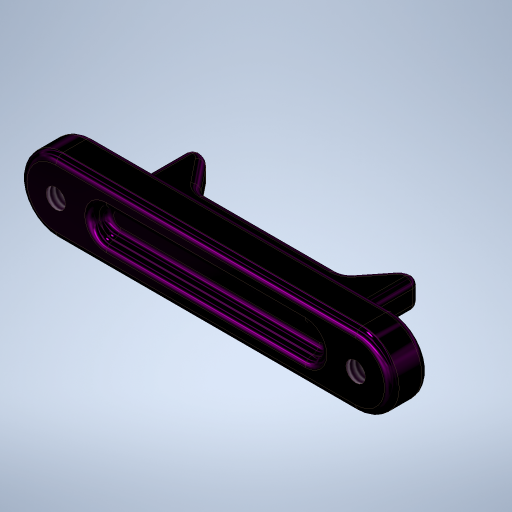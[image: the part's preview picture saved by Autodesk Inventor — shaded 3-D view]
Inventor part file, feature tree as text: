
AUTODESK INVENTOR PART (.ipt)
format: ipt  version: 2023.1 (Build 271208000, 208)  size: 450,560 bytes
history: native  units: in
note: dims shown in document units (in); Inventor stores cm internally (conversion verified against a paired STEP export)
features: sketch x4, extrude x3, fillet x3, other x2, hole x1, plane x1, projected_geometry x1
ambient origin geometry x8: Origin, YZ Plane, XZ Plane, XY Plane, X Axis, Y Axis, Z Axis, Center Point
bodies: Solid1 (feature_tree)
feature tree (15):
  extrude  "Extrusion1"  Depth=1.305in
  extrude  "Extrusion2"  Depth=0.865in
  hole  "Hole1"  [1 undecoded]
  plane  "Work Plane1"
  extrude  "Extrusion3"  Depth=0.275in
  fillet  "Fillet1"  Radius=0.0625in
  fillet  "Fillet2"  Radius=0.625in
  fillet  "Fillet3"  Radius=0.125in
  sketch  "Sketch1"  dims[d1=0.315in d2=1.305in]
  sketch  "Sketch2"  dims[d3=0.1625in d4=0.0in d5=0.865in]
  sketch  "Sketch3"  dims[d6=0.125in d7=0.0625in d8=0.0in]
  other  "Work Axis1"
  other  "Work Axis2"
  sketch  "Sketch4"  dims[d9=0.0849in d10=0.224in d11=0.375in d12=0.25in d13=0.5635in d14=0.349in d15=0.8108in d16=0.275in d17=0.0625in d18=0.625in d19=0.125in d20=0.315in d21=0.125in d22=0.0in d23=0.0625in d24=0.032in d25=0.032in]
  projected_geometry  "Project Cut Edges1"
note: 1 required parameter value undecoded (feature->parameter linkage not recoverable at this tier; creation-order binding heuristic only, values carry confidence <= 0.55)
